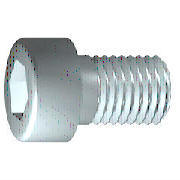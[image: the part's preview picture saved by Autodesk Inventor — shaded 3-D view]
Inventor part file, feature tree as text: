
AUTODESK INVENTOR PART (.ipt)
format: ipt  version: 2016 (Build 200138000, 138)  size: 198,656 bytes
history: native  units: mm (DEFAULTED — no unit token found)
features: sketch x2, extrude x1, plane x1, fillet x1
ambient origin geometry x7: Origin, YZ Plane, XY Plane, X Axis, Y Axis, Z Axis, Center Point
bodies: Solid1 (feature_tree), Body (feature_tree)
feature tree (5):
  extrude  "Slot"  Depth=3.0mm
  plane  "Work Plane1"
  fillet  "Fillet2"  Radius=3.0mm
  sketch  "Sketch1"  dims[d1=6.75mm d2=0.306825mm d3=3.0mm]
  sketch  "Sketch2"  dims[d4=1.3mm d5=60.0deg d6=3.0mm d7=3.0mm d8=2.886751mm d9=5.5mm d10=90.0deg d11=10.0mm d12=0.0mm d13=6.75mm d14=0.0mm d15=0.306725mm d16=0.306725mm d17=0.3mm d19=0.0mm d26=8.0mm d27=45.0deg d28=0.0mm d29=0.0mm d30=0.1mm]
